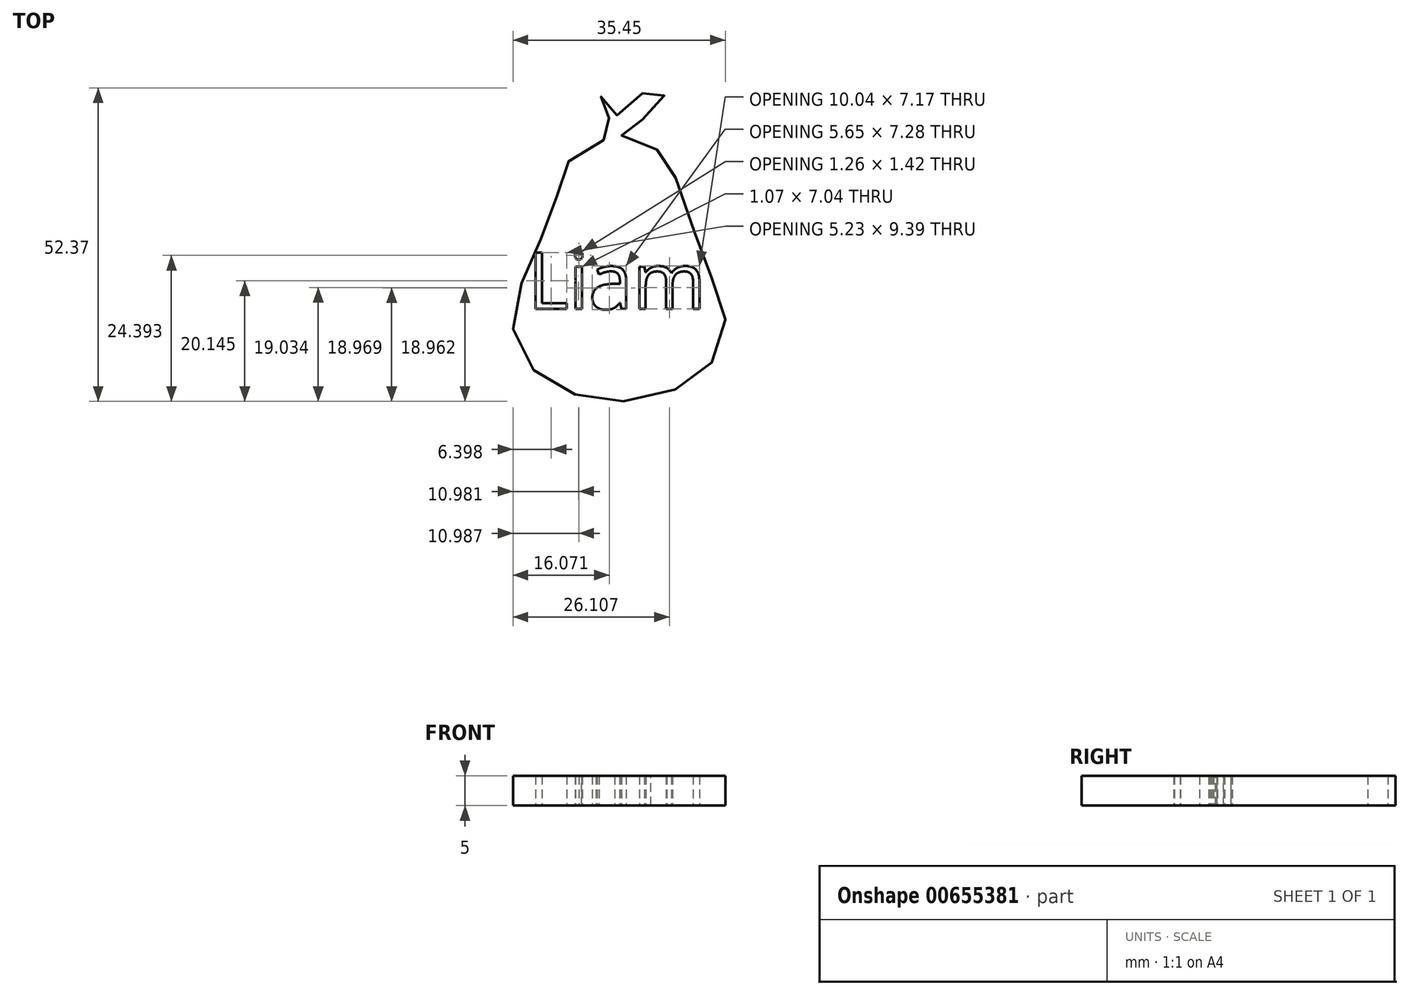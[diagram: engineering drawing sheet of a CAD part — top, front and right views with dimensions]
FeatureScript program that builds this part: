
annotation { "Feature Type Name" : "Feature", "Feature Type Description" : "" }
export const myFeature = defineFeature(function(context is Context, id is Id, definition is map)
    precondition{}
    {
        {
            var Q0;
            Q0=qCreatedBy(makeId("Top.planeOp"),FACE);
            var sketch = newSketch(context, id + "F0", { "sketchPlane" : qUnion([Q0])});
            skFitSpline(sketch, "E0", {"points": [v(-43.09, 49.82) * mm, v(-44.77, 45.15) * mm, v(-47.39, 38.79) * mm, v(-49.63, 33.56) * mm, v(-50.38, 27.76) * mm, v(-48.51, 22.53) * mm, v(-43.46, 18.23) * mm, v(-38.23, 16.17) * mm, v(-31.5, 15.6) * mm, v(-24.02, 17.3) * mm, v(-18.97, 19.9) * mm, v(-15.8, 24.96) * mm, v(-15.05, 29.82) * mm, v(-16.73, 34.5) * mm, v(-18.44, 40.47) * mm, v(-21.78, 47.39) * mm, v(-23.83, 54.68) * mm, v(-25.14, 56.36) * mm, v(-28.32, 58.8) * mm, v(-32.06, 59.73) * mm, v(-32.43, 61.6) * mm, v(-29.26, 62.53) * mm, v(-26.26, 64.21) * mm, v(-25.14, 66.64) * mm, v(-24.77, 67.77) * mm, v(-28.32, 67.2) * mm, v(-32.25, 64.21) * mm, v(-33, 63.28) * mm, v(-33.93, 65.52) * mm, v(-34.86, 66.64) * mm, v(-36.55, 65.7) * mm, v(-35.61, 64.21) * mm, v(-33.93, 62.16) * mm, v(-33.56, 59.91) * mm, v(-36.36, 58.98) * mm, v(-40.47, 56.74) * mm, v(-42.34, 52.06) * mm, v(-43.09, 49.82) * mm]});
            skText(sketch, "E1", { "text": "Liam", "fontName": "OpenSans-Regular.ttf"});
            const initialGuessF0  = {"E1": [-0.04793, 0.031, 1, 0, 0.00947]};
            skSetInitialGuess(sketch, initialGuessF0);
            skSolve(sketch);
        }
        {
            var Q0;
            Q0 = qSketchRegion(id + "F0", true);
            extrude(context, id + "F1", {"entities" : qUnion([Q0]), "depth" : 5 * mm, "offsetDistance" : 25.4 * mm});
        }
    });
